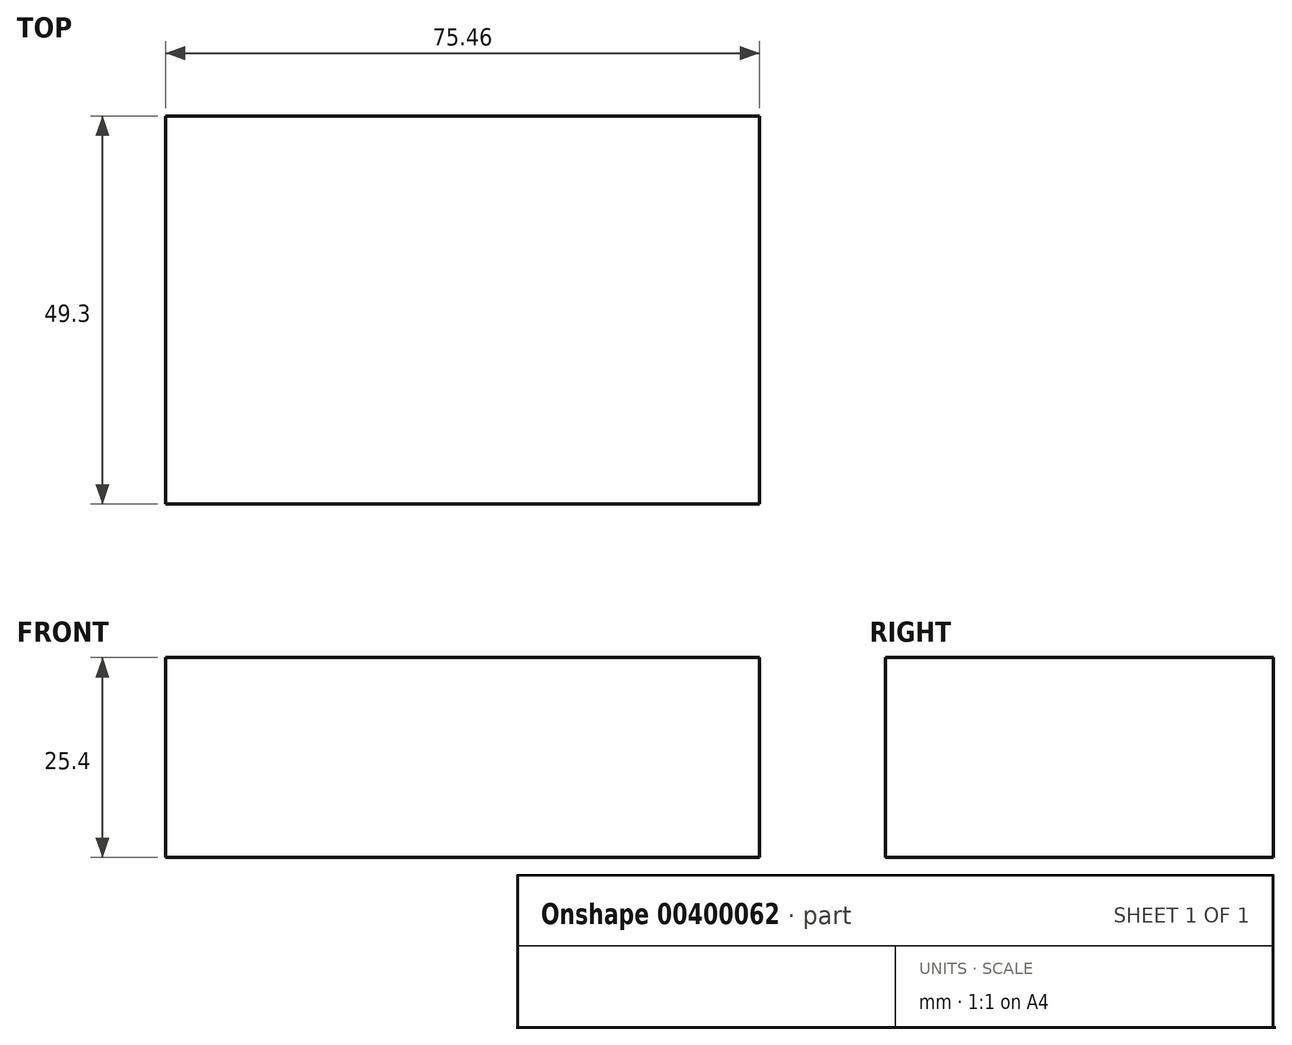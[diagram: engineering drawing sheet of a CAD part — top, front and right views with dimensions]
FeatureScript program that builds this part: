
annotation { "Feature Type Name" : "Feature", "Feature Type Description" : "" }
export const myFeature = defineFeature(function(context is Context, id is Id, definition is map)
    precondition{}
    {
        {
            var Q0;
            Q0=qCreatedBy(makeId("Top.planeOp"),FACE);
            var sketch = newSketch(context, id + "F0", { "sketchPlane" : qUnion([Q0])});
            skLineSegment(sketch, "E0.bottom", {"start": v(-36.06, 22.65) * mm, "end": v(39.4, 22.65) * mm});
            skLineSegment(sketch, "E0.top", {"start": v(-36.06, -26.65) * mm, "end": v(39.4, -26.65) * mm});
            skLineSegment(sketch, "E0.left", {"start": v(-36.06, 22.65) * mm, "end": v(-36.06, -26.65) * mm});
            skLineSegment(sketch, "E0.right", {"start": v(39.4, 22.65) * mm, "end": v(39.4, -26.65) * mm});
            skSolve(sketch);
        }
        {
            var Q0;
            Q0 = qSketchRegion(id + "F0", true);
            extrude(context, id + "F1", {"entities" : qUnion([Q0]), "depth" : 25.4 * mm});
        }
    });
